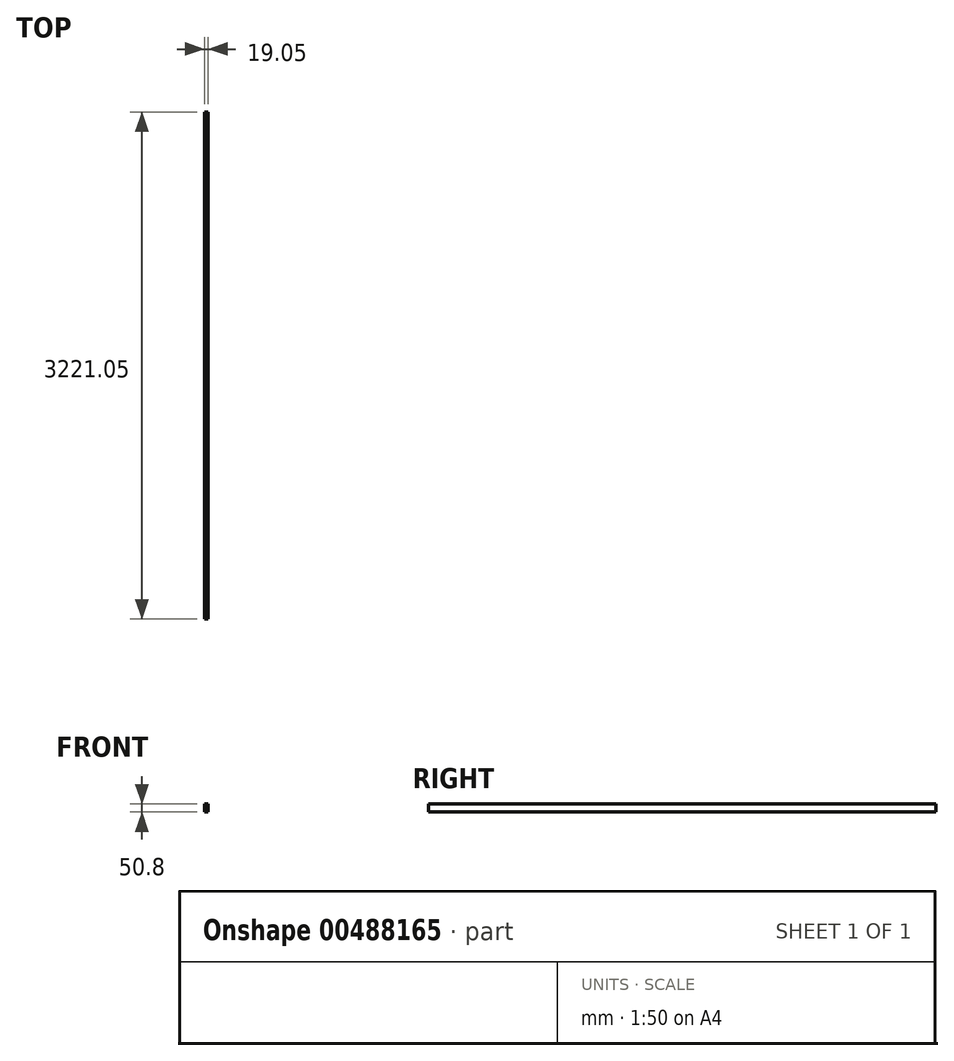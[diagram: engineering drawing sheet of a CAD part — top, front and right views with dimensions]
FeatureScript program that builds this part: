
annotation { "Feature Type Name" : "Feature", "Feature Type Description" : "" }
export const myFeature = defineFeature(function(context is Context, id is Id, definition is map)
    precondition{}
    {
        {
            var Q0;
            Q0=qCreatedBy(makeId("Front.planeOp"),FACE);
            var sketch = newSketch(context, id + "F0", { "sketchPlane" : qUnion([Q0])});
            skLineSegment(sketch, "E0", {"start": v(0, 0) * mm, "end": v(19.05, 0) * mm});
            skLineSegment(sketch, "E1", {"start": v(0, 0) * mm, "end": v(0, -50.8) * mm});
            skLineSegment(sketch, "E2", {"start": v(0, -50.8) * mm, "end": v(19.05, -50.8) * mm});
            skLineSegment(sketch, "E3", {"start": v(19.05, -50.8) * mm, "end": v(19.05, 0) * mm});
            skSolve(sketch);
        }
        {
            var Q0;
            Q0=makeQuery(id+"F0.imprint","IMPRINT",FACE,{"disambiguationData":[TD([[makeQuery(id+"F0.imprint","IMPRINT",EDGE,{"derivedFrom":sQuery(id+"F0.wireOp",EDGE,"E0")}),-1.0]])]});
            extrude(context, id + "F1", {"entities" : qUnion([Q0]), "oppositeDirection" : true, "depth" : 3221.05 * mm, "offsetDistance" : 25.4 * mm});
        }
    });
